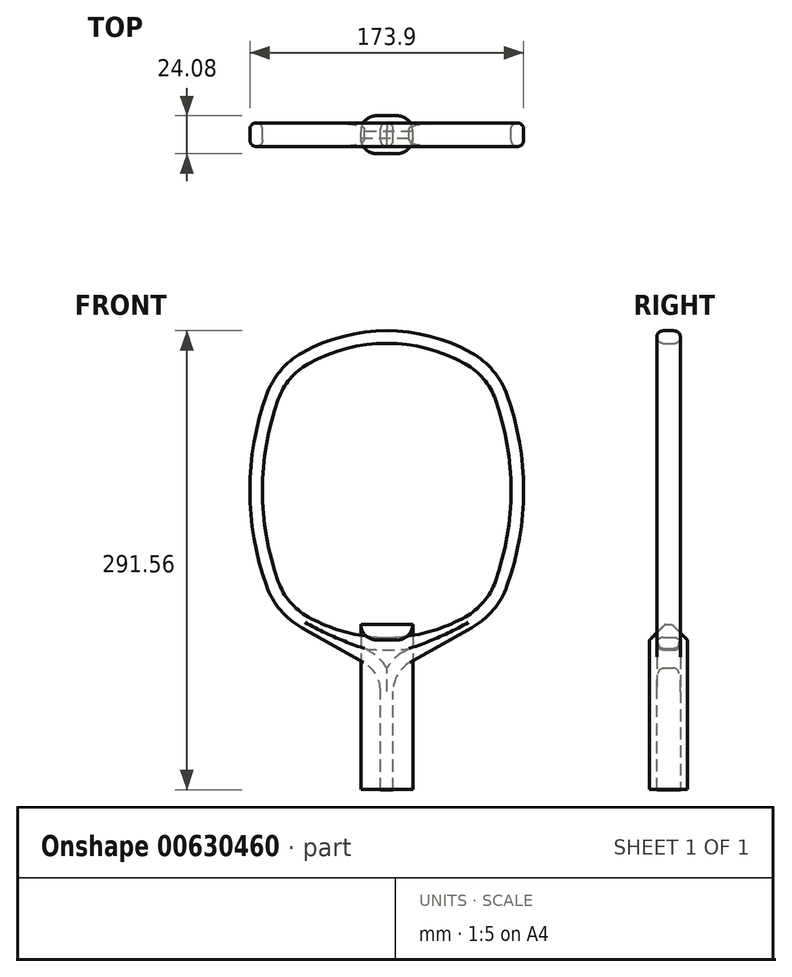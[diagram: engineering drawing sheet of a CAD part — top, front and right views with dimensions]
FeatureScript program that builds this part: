
annotation { "Feature Type Name" : "Feature", "Feature Type Description" : "" }
export const myFeature = defineFeature(function(context is Context, id is Id, definition is map)
    precondition{}
    {
        {
            var Q0;
            Q0=qCreatedBy(makeId("Front.planeOp"),FACE);
            var sketch = newSketch(context, id + "F0", { "sketchPlane" : qUnion([Q0])});
            skLineSegment(sketch, "E0.bottom", {"start": v(70, 76.25) * mm, "end": v(-70, 76.25) * mm, "construction": true});
            skLineSegment(sketch, "E0.top", {"start": v(70, -76.25) * mm, "end": v(-70, -76.25) * mm, "construction": true});
            skLineSegment(sketch, "E0.left", {"start": v(70, 76.25) * mm, "end": v(70, -76.25) * mm, "construction": true});
            skLineSegment(sketch, "E0.right", {"start": v(-70, 76.25) * mm, "end": v(-70, -76.25) * mm, "construction": true});
            skPoint(sketch, "E0.middle", {"position": v(0, 0) * mm});
            skArc(sketch, "E1", {"start": v(53.86, 87.3) * mm, "mid": v(0, 101.4) * mm, "end": v(-53.86, 87.3) * mm});
            skArc(sketch, "E2", {"start": v(-53.86, -87.3) * mm, "mid": v(0, -101.4) * mm, "end": v(53.86, -87.3) * mm});
            skArc(sketch, "E3", {"start": v(76.47, -60.53) * mm, "mid": v(86.95, 0) * mm, "end": v(76.47, 60.53) * mm});
            skArc(sketch, "E4", {"start": v(-76.47, 60.53) * mm, "mid": v(-86.95, 0) * mm, "end": v(-76.47, -60.53) * mm});
            skPoint(sketch, "E5.visualSharp", {"position": v(70, 76.25) * mm});
            skArc(sketch, "E5.filletArc", {"start": v(76.47, 60.53) * mm, "mid": v(67.59, 75.96) * mm, "end": v(53.86, 87.3) * mm});
            skPoint(sketch, "E6.visualSharp", {"position": v(-70, 76.25) * mm});
            skArc(sketch, "E6.filletArc", {"start": v(-53.86, 87.3) * mm, "mid": v(-67.59, 75.96) * mm, "end": v(-76.47, 60.53) * mm});
            skPoint(sketch, "E7.visualSharp", {"position": v(-70, -76.25) * mm});
            skArc(sketch, "E7.filletArc", {"start": v(-76.47, -60.53) * mm, "mid": v(-67.59, -75.96) * mm, "end": v(-53.86, -87.3) * mm});
            skPoint(sketch, "E8.visualSharp", {"position": v(70, -76.25) * mm});
            skArc(sketch, "E8.filletArc", {"start": v(53.86, -87.3) * mm, "mid": v(67.59, -75.96) * mm, "end": v(76.47, -60.53) * mm});
            skSolve(sketch);
        }
        {
            var Q0;
            Q0=makeQuery(id+"F0.imprint","IMPRINT",FACE,{"disambiguationData":[TD([[makeQuery(id+"F0.imprint","IMPRINT",EDGE,{"derivedFrom":sQuery(id+"F0.wireOp",EDGE,"E1")}),1.0]])]});
            extrude(context, id + "F1", {"entities" : qUnion([Q0]), "endBound" : BoundingType.SYMMETRIC, "depth" : 15 * mm, "offsetDistance" : 25 * mm});
        }
        {
            var Q0;
            Q0=makeQuery(id+"F1.opExtrude","CAP_FACE",FACE,{"disambiguationData":[OSD([sQuery(id+"F0.wireOp",EDGE,"E1"),sQuery(id+"F0.wireOp",EDGE,"E2"),sQuery(id+"F0.wireOp",EDGE,"E3"),sQuery(id+"F0.wireOp",EDGE,"E4"),sQuery(id+"F0.wireOp",EDGE,"E5.filletArc"),sQuery(id+"F0.wireOp",EDGE,"E6.filletArc"),sQuery(id+"F0.wireOp",EDGE,"E7.filletArc"),sQuery(id+"F0.wireOp",EDGE,"E8.filletArc")])],"isStart":false});
            var Q1;
            Q1=makeQuery(id+"F1.opExtrude","CAP_FACE",FACE,{"disambiguationData":[OSD([sQuery(id+"F0.wireOp",EDGE,"E1"),sQuery(id+"F0.wireOp",EDGE,"E2"),sQuery(id+"F0.wireOp",EDGE,"E3"),sQuery(id+"F0.wireOp",EDGE,"E4"),sQuery(id+"F0.wireOp",EDGE,"E5.filletArc"),sQuery(id+"F0.wireOp",EDGE,"E6.filletArc"),sQuery(id+"F0.wireOp",EDGE,"E7.filletArc"),sQuery(id+"F0.wireOp",EDGE,"E8.filletArc")])],"isStart":true});
            shell(context, id + "F2", {"entities" : qUnion([Q0, Q1]), "thickness" : 8 * mm});
        }
        {
            var Q0;
            Q0=qCreatedBy(makeId("Top.planeOp"),FACE);
            cPlane(context, id + "F3", {"entities" : qUnion([Q0]), "cplaneType" : CPlaneType.OFFSET, "offset" : 190 * mm, "oppositeDirection" : true, "width" : 150 * mm, "height" : 150 * mm});
        }
        {
            var Q0;
            Q0=qCreatedBy(id+"F3.planeOp",FACE);
            var sketch = newSketch(context, id + "F4", { "sketchPlane" : qUnion([Q0])});
            skPoint(sketch, "E9.0", {"position": v(0, 0) * mm});
            skLineSegment(sketch, "E10.bottom", {"start": v(4, -7.5) * mm, "end": v(-4, -7.5) * mm});
            skLineSegment(sketch, "E10.top", {"start": v(4, 7.5) * mm, "end": v(-4, 7.5) * mm});
            skLineSegment(sketch, "E10.left", {"start": v(4, -7.5) * mm, "end": v(4, 7.5) * mm});
            skLineSegment(sketch, "E10.right", {"start": v(-4, -7.5) * mm, "end": v(-4, 7.5) * mm});
            skSolve(sketch);
        }
        {
            var Q0;
            Q0=qCreatedBy(makeId("Front.planeOp"),FACE);
            var sketch = newSketch(context, id + "F5", { "sketchPlane" : qUnion([Q0])});
            skArc(sketch, "E11.0.0", {"start": v(-76.47, -60.53) * mm, "mid": v(-67.59, -75.96) * mm, "end": v(-53.86, -87.3) * mm});
            skArc(sketch, "E11.0.1", {"start": v(-53.86, -87.3) * mm, "mid": v(0, -101.4) * mm, "end": v(53.86, -87.3) * mm});
            skArc(sketch, "E11.0.2", {"start": v(53.86, -87.3) * mm, "mid": v(67.59, -75.96) * mm, "end": v(76.47, -60.53) * mm});
            skArc(sketch, "E11.0.3", {"start": v(76.47, -60.53) * mm, "mid": v(86.95, 0) * mm, "end": v(76.47, 60.53) * mm});
            skArc(sketch, "E11.0.4", {"start": v(76.47, 60.53) * mm, "mid": v(67.59, 75.96) * mm, "end": v(53.86, 87.3) * mm});
            skArc(sketch, "E11.0.5", {"start": v(53.86, 87.3) * mm, "mid": v(0, 101.4) * mm, "end": v(-53.86, 87.3) * mm});
            skArc(sketch, "E11.0.6", {"start": v(-53.86, 87.3) * mm, "mid": v(-67.59, 75.96) * mm, "end": v(-76.47, 60.53) * mm});
            skArc(sketch, "E11.0.7", {"start": v(-76.47, 60.53) * mm, "mid": v(-86.95, 0) * mm, "end": v(-76.47, -60.53) * mm});
            skArc(sketch, "E12.0", {"start": v(-49.94, -80.33) * mm, "mid": v(0, -93.4) * mm, "end": v(49.94, -80.33) * mm});
            skLineSegment(sketch, "E13", {"start": v(-53.86, -87.3) * mm, "end": v(-49.94, -80.33) * mm});
            skLineSegment(sketch, "E14", {"start": v(49.94, -80.33) * mm, "end": v(53.86, -87.3) * mm});
            skLineSegment(sketch, "E15", {"start": v(-51.9, -83.82) * mm, "end": v(-12.76, -105.8) * mm});
            skLineSegment(sketch, "E16", {"start": v(51.9, -83.82) * mm, "end": v(12.76, -105.8) * mm});
            skLineSegment(sketch, "E17", {"start": v(0, -190.16) * mm, "end": v(0, -127.6) * mm});
            skPoint(sketch, "E18.visualSharp", {"position": v(0, -112.97) * mm});
            skArc(sketch, "E18.filletArc", {"start": v(12.76, -105.8) * mm, "mid": v(3.42, -114.97) * mm, "end": v(0, -127.6) * mm});
            skArc(sketch, "E19.filletArc", {"start": v(0, -127.6) * mm, "mid": v(-3.42, -114.97) * mm, "end": v(-12.76, -105.8) * mm});
            skSolve(sketch);
        }
        {
            var Q0;
            Q0=makeQuery(id+"F4.imprint","IMPRINT",FACE,{"disambiguationData":[TD([[makeQuery(id+"F4.imprint","IMPRINT",EDGE,{"derivedFrom":sQuery(id+"F4.wireOp",EDGE,"E10.bottom")}),-1.0]])]});
            var Q1;
            Q1=sQuery(id+"F5.wireOp",EDGE,"E17");
            var Q2;
            Q2=sQuery(id+"F5.wireOp",EDGE,"E19.filletArc");
            var Q3;
            Q3=sQuery(id+"F5.wireOp",EDGE,"E15");
            sweep(context, id + "F6", {"operationType" : NewBodyOperationType.ADD, "profiles" : qUnion([Q0]), "path" : qUnion([Q1, Q2, Q3])});
        }
        {
            var Q0;
            Q0=makeQuery(id+"F6.opSweep","CAP_FACE",FACE,{"disambiguationData":[OSD([sQuery(id+"F4.wireOp",EDGE,"E10.bottom"),sQuery(id+"F4.wireOp",EDGE,"E10.top"),sQuery(id+"F4.wireOp",EDGE,"E10.left"),sQuery(id+"F4.wireOp",EDGE,"E10.right"),sQuery(id+"F5.wireOp",VERTEX,"E17.start")])],"isStart":true});
            var Q1;
            Q1=sQuery(id+"F5.wireOp",EDGE,"E17");
            var Q2;
            Q2=sQuery(id+"F5.wireOp",EDGE,"E18.filletArc");
            var Q3;
            Q3=sQuery(id+"F5.wireOp",EDGE,"E16");
            sweep(context, id + "F7", {"operationType" : NewBodyOperationType.ADD, "profiles" : qUnion([Q0]), "path" : qUnion([Q1, Q2, Q3])});
        }
        {
            var Q0;
            Q0=makeQuery(id+"F1.opExtrude","CAP_EDGE",EDGE,{"disambiguationData":[OSD([sQuery(id+"F0.wireOp",EDGE,"E4")])],"isStart":false});
            var Q1;
            Q1=makeQuery(id+"F7.opSweep","SWEPT_EDGE",EDGE,{"disambiguationData":[OSD([sQuery(id+"F4.wireOp",EDGE,"E10.top"),sQuery(id+"F4.wireOp",EDGE,"E10.left"),sQuery(id+"F5.wireOp",EDGE,"E16"),sQuery(id+"F5.wireOp",EDGE,"E17")])]});
            var Q2;
            {var subQ0=sQuery(id+"F0.wireOp",EDGE,"E8.filletArc");Q2=makeQuery(id+"F2.opShell","OFFSET_EDGE",EDGE,{"disambiguationData":[OSD([subQ0]),TDD([makeQuery(id+"F1.opExtrude","CAP_EDGE",EDGE,{"disambiguationData":[OSD([subQ0])],"isStart":true})])]});}
            var Q3;
            {var subQ0=sQuery(id+"F0.wireOp",EDGE,"E8.filletArc");Q3=makeQuery(id+"F2.opShell","OFFSET_EDGE",EDGE,{"disambiguationData":[OSD([subQ0]),TDD([makeQuery(id+"F1.opExtrude","CAP_EDGE",EDGE,{"disambiguationData":[OSD([subQ0])],"isStart":false})])]});}
            var Q4;
            Q4=makeQuery(id+"F7.opSweep","SWEPT_EDGE",EDGE,{"disambiguationData":[OSD([sQuery(id+"F4.wireOp",EDGE,"E10.top"),sQuery(id+"F4.wireOp",EDGE,"E10.right"),sQuery(id+"F5.wireOp",EDGE,"E17"),sQuery(id+"F5.wireOp",EDGE,"E18.filletArc")])]});
            var Q5;
            Q5=makeQuery(id+"F6.opSweep","SWEPT_EDGE",EDGE,{"disambiguationData":[OSD([sQuery(id+"F4.wireOp",EDGE,"E10.top"),sQuery(id+"F4.wireOp",EDGE,"E10.left"),sQuery(id+"F5.wireOp",EDGE,"E19.filletArc")])]});
            var Q6;
            Q6=makeQuery(id+"F1.opExtrude","CAP_EDGE",EDGE,{"disambiguationData":[OSD([sQuery(id+"F0.wireOp",EDGE,"E2")])],"isStart":true});
            var Q7;
            Q7=makeQuery(id+"F1.opExtrude","CAP_EDGE",EDGE,{"disambiguationData":[OSD([sQuery(id+"F0.wireOp",EDGE,"E2")])],"isStart":false});
            var Q8;
            Q8=makeQuery(id+"F6.opSweep","SWEPT_EDGE",EDGE,{"disambiguationData":[OSD([sQuery(id+"F4.wireOp",EDGE,"E10.bottom"),sQuery(id+"F4.wireOp",EDGE,"E10.left"),sQuery(id+"F5.wireOp",EDGE,"E19.filletArc")])]});
            var Q9;
            Q9=makeQuery(id+"F7.opSweep","SWEPT_EDGE",EDGE,{"disambiguationData":[OSD([sQuery(id+"F4.wireOp",EDGE,"E10.bottom"),sQuery(id+"F4.wireOp",EDGE,"E10.right"),sQuery(id+"F5.wireOp",EDGE,"E17"),sQuery(id+"F5.wireOp",EDGE,"E18.filletArc")])]});
            fillet(context, id + "F8", {"entities" : qUnion([Q0, Q1, Q2, Q3, Q4, Q5, Q6, Q7, Q8, Q9]), "radius" : 4 * mm, "tangentPropagation" : true, "allowEdgeOverflow" : false});
        }
        {
            var Q0;
            Q0=qCreatedBy(id+"F3.planeOp",FACE);
            var sketch = newSketch(context, id + "F9", { "sketchPlane" : qUnion([Q0])});
            skLineSegment(sketch, "E20.bottom", {"start": v(16.52, -12.04) * mm, "end": v(-16.52, -12.04) * mm});
            skLineSegment(sketch, "E20.top", {"start": v(16.52, 12.04) * mm, "end": v(-16.52, 12.04) * mm});
            skLineSegment(sketch, "E20.left", {"start": v(16.52, -12.04) * mm, "end": v(16.52, 12.04) * mm});
            skLineSegment(sketch, "E20.right", {"start": v(-16.52, -12.04) * mm, "end": v(-16.52, 12.04) * mm});
            skPoint(sketch, "E20.middle", {"position": v(0, 0) * mm});
            skSolve(sketch);
        }
        {
            var Q0;
            Q0=makeQuery(id+"F9.imprint","IMPRINT",FACE,{"disambiguationData":[TD([[makeQuery(id+"F9.imprint","IMPRINT",EDGE,{"derivedFrom":sQuery(id+"F9.wireOp",EDGE,"E20.bottom")}),-1.0]])]});
            extrude(context, id + "F10", {"entities" : qUnion([Q0]), "depth" : 105 * mm, "offsetDistance" : 25 * mm});
        }
        {
            var Q0;
            Q0=makeQuery(id+"F10.opExtrude","CAP_EDGE",EDGE,{"disambiguationData":[OSD([sQuery(id+"F9.wireOp",EDGE,"E20.bottom")])],"isStart":false});
            var Q1;
            Q1=makeQuery(id+"F10.opExtrude","CAP_EDGE",EDGE,{"disambiguationData":[OSD([sQuery(id+"F9.wireOp",EDGE,"E20.top")])],"isStart":false});
            chamfer(context, id + "F11", {"entities" : qUnion([Q0, Q1]), "width" : 10 * mm, "tangentPropagation" : true});
        }
        {
            var Q0;
            Q0=makeQuery(id+"F10.opExtrude","SWEPT_EDGE",EDGE,{"disambiguationData":[OSD([sQuery(id+"F9.wireOp",EDGE,"E20.bottom"),sQuery(id+"F9.wireOp",EDGE,"E20.right")])]});
            var Q1;
            Q1=makeQuery(id+"F10.opExtrude","SWEPT_EDGE",EDGE,{"disambiguationData":[OSD([sQuery(id+"F9.wireOp",EDGE,"E20.top"),sQuery(id+"F9.wireOp",EDGE,"E20.right")])]});
            var Q2;
            Q2=makeQuery(id+"F10.opExtrude","SWEPT_EDGE",EDGE,{"disambiguationData":[OSD([sQuery(id+"F9.wireOp",EDGE,"E20.top"),sQuery(id+"F9.wireOp",EDGE,"E20.left")])]});
            var Q3;
            Q3=makeQuery(id+"F10.opExtrude","SWEPT_EDGE",EDGE,{"disambiguationData":[OSD([sQuery(id+"F9.wireOp",EDGE,"E20.bottom"),sQuery(id+"F9.wireOp",EDGE,"E20.left")])]});
            fillet(context, id + "F12", {"entities" : qUnion([Q0, Q1, Q2, Q3]), "radius" : 10 * mm, "tangentPropagation" : true, "allowEdgeOverflow" : false});
        }
    });
